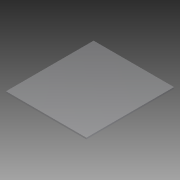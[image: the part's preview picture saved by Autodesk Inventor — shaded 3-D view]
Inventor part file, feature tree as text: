
AUTODESK INVENTOR PART (.ipt)
format: ipt  version: 2015 (Build 190159000, 159)  size: 74,752 bytes
history: native  units: mm
features: reference x4, extrude x1, sketch x1
ambient origin geometry x8: Origin, YZ Plane, XZ Plane, XY Plane, X Axis, Y Axis, Z Axis, Center Point
bodies: Solid1 (feature_tree)
feature tree (6):
  extrude  "Extrusion1"  Depth=4.0mm
  sketch  "Sketch1"  dims[d0=1.0mm d1=1.0mm d2=1.0mm d3=1.0mm d4=4.0mm d5=0.0mm]
  reference  "Reference1"
  reference  "Reference2"
  reference  "Reference3"
  reference  "Reference4"
